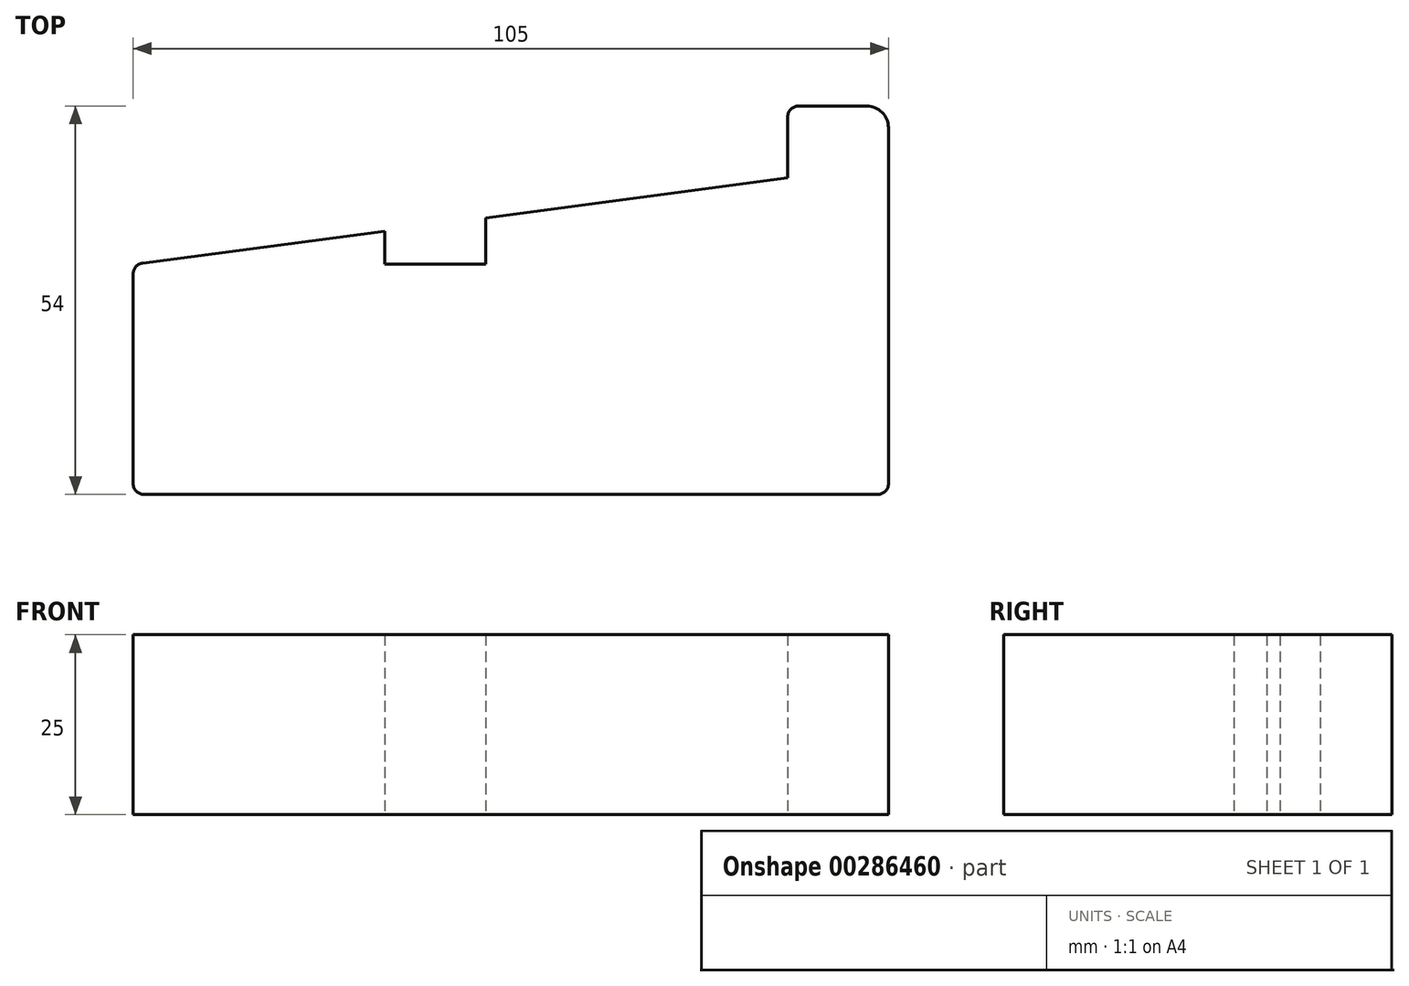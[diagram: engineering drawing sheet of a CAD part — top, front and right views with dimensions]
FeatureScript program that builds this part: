
annotation { "Feature Type Name" : "Feature", "Feature Type Description" : "" }
export const myFeature = defineFeature(function(context is Context, id is Id, definition is map)
    precondition{}
    {
        {
            var Q0;
            Q0=qCreatedBy(makeId("Top.planeOp"),FACE);
            var sketch = newSketch(context, id + "F0", { "sketchPlane" : qUnion([Q0])});
            skLineSegment(sketch, "E0", {"start": v(-70.2, -20.4) * mm, "end": v(31.8, -20.4) * mm});
            skLineSegment(sketch, "E1", {"start": v(33.3, -18.9) * mm, "end": v(33.3, 30.6) * mm});
            skLineSegment(sketch, "E2", {"start": v(30.3, 33.6) * mm, "end": v(20.8, 33.6) * mm});
            skLineSegment(sketch, "E3", {"start": v(19.3, 32.1) * mm, "end": v(19.3, 23.6) * mm});
            skLineSegment(sketch, "E4", {"start": v(-71.7, -18.9) * mm, "end": v(-71.7, 10.29) * mm});
            skPoint(sketch, "E5.visualSharp", {"position": v(-71.7, -20.4) * mm});
            skArc(sketch, "E5.filletArc", {"start": v(-71.7, -18.9) * mm, "mid": v(-71.25, -19.96) * mm, "end": v(-70.2, -20.4) * mm});
            skLineSegment(sketch, "E6", {"start": v(-70.39, 11.78) * mm, "end": v(-36.7, 16.22) * mm});
            skLineSegment(sketch, "E7", {"start": v(-36.7, 16.22) * mm, "end": v(-36.7, 11.6) * mm});
            skLineSegment(sketch, "E8", {"start": v(-36.7, 11.6) * mm, "end": v(-22.7, 11.6) * mm});
            skLineSegment(sketch, "E9", {"start": v(-22.7, 11.6) * mm, "end": v(-22.7, 18.07) * mm});
            skLineSegment(sketch, "E10.trimOffspring", {"start": v(-22.7, 18.07) * mm, "end": v(19.3, 23.6) * mm});
            skPoint(sketch, "E11.visualSharp", {"position": v(-71.7, 11.6) * mm});
            skArc(sketch, "E11.filletArc", {"start": v(-70.39, 11.78) * mm, "mid": v(-71.32, 11.28) * mm, "end": v(-71.7, 10.29) * mm});
            skPoint(sketch, "E12.visualSharp", {"position": v(33.3, -20.4) * mm});
            skArc(sketch, "E12.filletArc", {"start": v(31.8, -20.4) * mm, "mid": v(32.87, -19.96) * mm, "end": v(33.3, -18.9) * mm});
            skPoint(sketch, "E13.visualSharp", {"position": v(19.3, 33.6) * mm});
            skArc(sketch, "E13.filletArc", {"start": v(20.8, 33.6) * mm, "mid": v(19.75, 33.16) * mm, "end": v(19.3, 32.1) * mm});
            skPoint(sketch, "E14.visualSharp", {"position": v(33.3, 33.6) * mm});
            skArc(sketch, "E14.filletArc", {"start": v(33.3, 30.6) * mm, "mid": v(32.43, 32.73) * mm, "end": v(30.3, 33.6) * mm});
            skSolve(sketch);
        }
        {
            var Q0;
            Q0=makeQuery(id+"F0.imprint","IMPRINT",FACE,{"disambiguationData":[TD([[makeQuery(id+"F0.imprint","IMPRINT",EDGE,{"derivedFrom":sQuery(id+"F0.wireOp",EDGE,"E0")}),1.0]])]});
            extrude(context, id + "F1", {"entities" : qUnion([Q0]), "depth" : 25 * mm});
        }
    });
